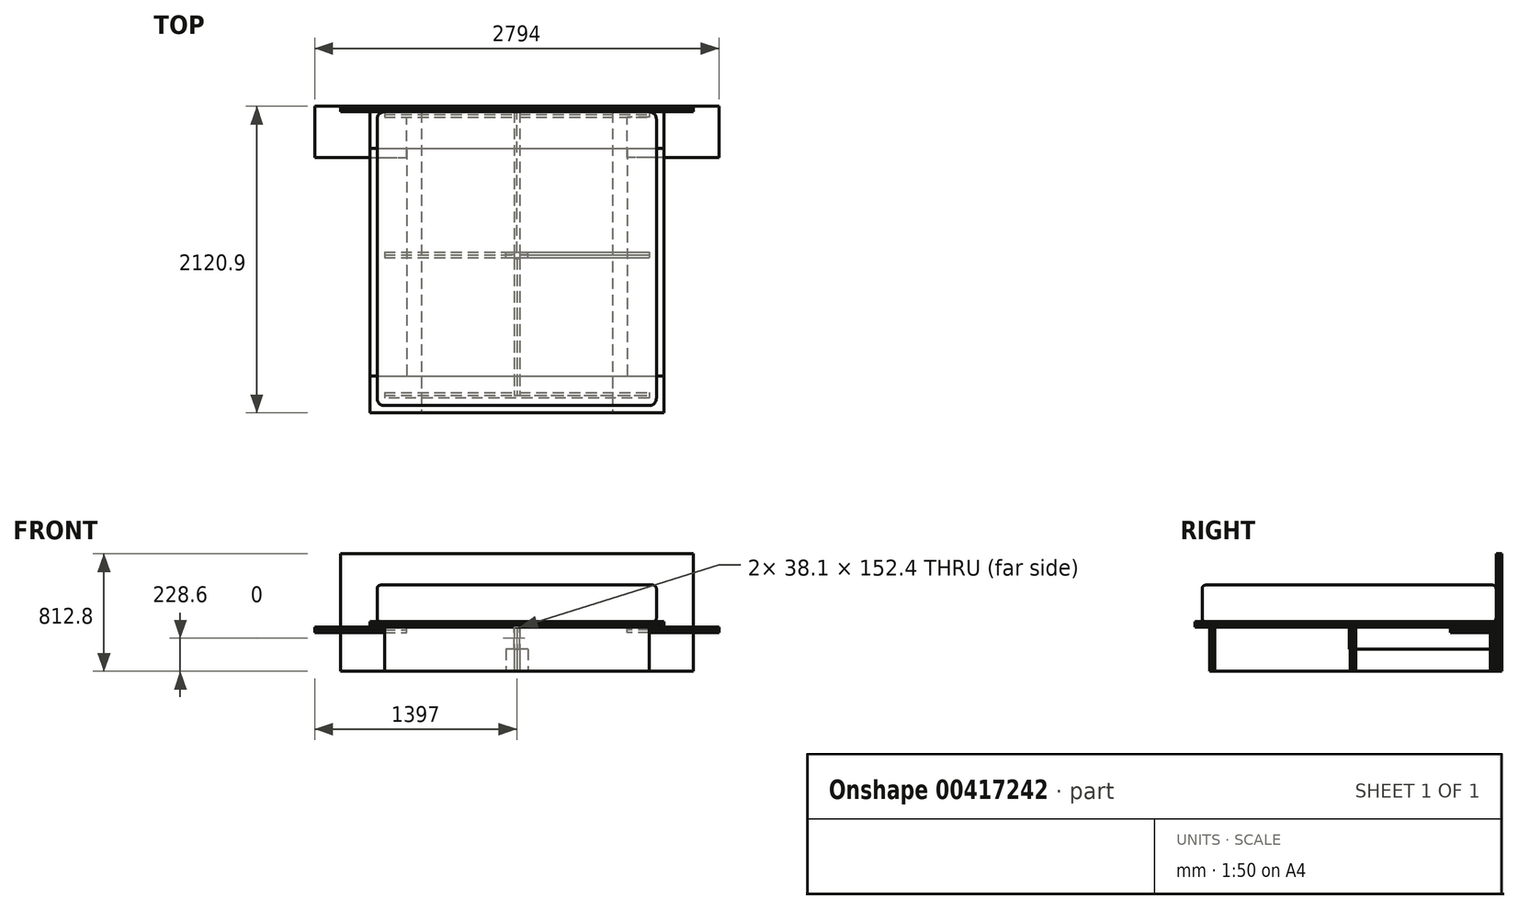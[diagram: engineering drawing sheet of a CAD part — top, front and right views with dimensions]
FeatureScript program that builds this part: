
annotation { "Feature Type Name" : "Feature", "Feature Type Description" : "" }
export const myFeature = defineFeature(function(context is Context, id is Id, definition is map)
    precondition{}
    {
        {
            var Q0;
            Q0=qCreatedBy(makeId("Top.planeOp"),FACE);
            var sketch = newSketch(context, id + "F0", { "sketchPlane" : qUnion([Q0])});
            skLineSegment(sketch, "E0.bottom", {"start": v(-965.2, 1016) * mm, "end": v(965.2, 1016) * mm});
            skLineSegment(sketch, "E0.top", {"start": v(-965.2, -1016) * mm, "end": v(965.2, -1016) * mm});
            skLineSegment(sketch, "E0.left", {"start": v(-965.2, 1016) * mm, "end": v(-965.2, -1016) * mm});
            skLineSegment(sketch, "E0.right", {"start": v(965.2, 1016) * mm, "end": v(965.2, -1016) * mm});
            skPoint(sketch, "E0.middle", {"position": v(0, 0) * mm});
            skLineSegment(sketch, "E1", {"start": v(0, 1016) * mm, "end": v(0, -1016) * mm, "construction": true});
            skSolve(sketch);
        }
        {
            var Q0;
            Q0=qCreatedBy(makeId("Top.planeOp"),FACE);
            var sketch = newSketch(context, id + "F1", { "sketchPlane" : qUnion([Q0])});
            skLineSegment(sketch, "E2.bottom", {"start": v(-1219.2, 1035.05) * mm, "end": v(1219.2, 1035.05) * mm});
            skLineSegment(sketch, "E2.top", {"start": v(-1219.2, 1016) * mm, "end": v(1219.2, 1016) * mm});
            skLineSegment(sketch, "E2.left", {"start": v(-1219.2, 1035.05) * mm, "end": v(-1219.2, 1016) * mm});
            skLineSegment(sketch, "E2.right", {"start": v(1219.2, 1035.05) * mm, "end": v(1219.2, 1016) * mm});
            skLineSegment(sketch, "E3", {"start": v(0, 1035.05) * mm, "end": v(0, 1016) * mm, "construction": true});
            skLineSegment(sketch, "E4.top", {"start": v(-1219.2, 1054.1) * mm, "end": v(1219.2, 1054.1) * mm});
            skLineSegment(sketch, "E4.left", {"start": v(-1219.2, 1035.05) * mm, "end": v(-1219.2, 1054.1) * mm});
            skLineSegment(sketch, "E4.right", {"start": v(1219.2, 1035.05) * mm, "end": v(1219.2, 1054.1) * mm});
            skSolve(sketch);
        }
        {
            var Q0;
            Q0=qCreatedBy(makeId("Top.planeOp"),FACE);
            var sketch = newSketch(context, id + "F2", { "sketchPlane" : qUnion([Q0])});
            skLineSegment(sketch, "E5.bottom", {"start": v(-1016, 1016) * mm, "end": v(1016, 1016) * mm});
            skLineSegment(sketch, "E5.top", {"start": v(-1016, -1066.8) * mm, "end": v(1016, -1066.8) * mm});
            skLineSegment(sketch, "E5.left", {"start": v(-1016, 1016) * mm, "end": v(-1016, -1066.8) * mm});
            skLineSegment(sketch, "E5.right", {"start": v(1016, 1016) * mm, "end": v(1016, -1066.8) * mm});
            skLineSegment(sketch, "E6", {"start": v(0, 1016) * mm, "end": v(0, -1066.8) * mm, "construction": true});
            skLineSegment(sketch, "E7", {"start": v(-1016, 762) * mm, "end": v(1016, 762) * mm, "construction": true});
            skLineSegment(sketch, "E8", {"start": v(-762, 1016) * mm, "end": v(-762, -1066.8) * mm, "construction": true});
            skLineSegment(sketch, "E9", {"start": v(-1016, -812.8) * mm, "end": v(1016, -812.8) * mm, "construction": true});
            skLineSegment(sketch, "E10", {"start": v(762, 1016) * mm, "end": v(762, -1066.8) * mm, "construction": true});
            skSolve(sketch);
        }
        {
            var Q0;
            Q0=qCreatedBy(makeId("Top.planeOp"),FACE);
            var sketch = newSketch(context, id + "F3", { "sketchPlane" : qUnion([Q0])});
            skLineSegment(sketch, "E11.bottom", {"start": v(-1397, 698.5) * mm, "end": v(-762, 698.5) * mm});
            skLineSegment(sketch, "E11.top", {"start": v(-1397, 1054.1) * mm, "end": v(-762, 1054.1) * mm});
            skLineSegment(sketch, "E11.left", {"start": v(-1397, 698.5) * mm, "end": v(-1397, 1054.1) * mm});
            skLineSegment(sketch, "E11.right", {"start": v(-762, 698.5) * mm, "end": v(-762, 1054.1) * mm});
            skLineSegment(sketch, "E12.MirrorCS", {"start": v(1397, 1054.1) * mm, "end": v(762, 1054.1) * mm});
            skLineSegment(sketch, "E13.MirrorCS", {"start": v(1397, 698.5) * mm, "end": v(1397, 1054.1) * mm});
            skLineSegment(sketch, "E14.MirrorCS", {"start": v(1397, 698.5) * mm, "end": v(762, 698.5) * mm});
            skLineSegment(sketch, "E15.MirrorCS", {"start": v(762, 698.5) * mm, "end": v(762, 1054.1) * mm});
            skSolve(sketch);
        }
        {
            var Q0;
            Q0=qCreatedBy(makeId("Top.planeOp"),FACE);
            var sketch = newSketch(context, id + "F4", { "sketchPlane" : qUnion([Q0])});
            skLineSegment(sketch, "E16.bottom", {"start": v(-914.4, 996.95) * mm, "end": v(914.4, 996.95) * mm});
            skLineSegment(sketch, "E16.top", {"start": v(-914.4, 1016) * mm, "end": v(914.4, 1016) * mm});
            skLineSegment(sketch, "E16.left", {"start": v(-914.4, 1016) * mm, "end": v(-914.4, 996.95) * mm});
            skLineSegment(sketch, "E16.right", {"start": v(914.4, 1016) * mm, "end": v(914.4, 996.95) * mm});
            skLineSegment(sketch, "E17", {"start": v(0, 1016) * mm, "end": v(0, 996.95) * mm, "construction": true});
            skLineSegment(sketch, "E18.top", {"start": v(-914.4, 977.9) * mm, "end": v(914.4, 977.9) * mm});
            skLineSegment(sketch, "E18.left", {"start": v(-914.4, 996.95) * mm, "end": v(-914.4, 977.9) * mm});
            skLineSegment(sketch, "E18.right", {"start": v(914.4, 996.95) * mm, "end": v(914.4, 977.9) * mm});
            skLineSegment(sketch, "E19.bottom", {"start": v(-914.4, 44.45) * mm, "end": v(914.4, 44.45) * mm});
            skLineSegment(sketch, "E19.top", {"start": v(-914.4, 25.4) * mm, "end": v(914.4, 25.4) * mm});
            skLineSegment(sketch, "E19.left", {"start": v(-914.4, 44.45) * mm, "end": v(-914.4, 25.4) * mm});
            skLineSegment(sketch, "E19.right", {"start": v(914.4, 44.45) * mm, "end": v(914.4, 25.4) * mm});
            skLineSegment(sketch, "E20.top", {"start": v(-914.4, 6.35) * mm, "end": v(914.4, 6.35) * mm});
            skLineSegment(sketch, "E20.left", {"start": v(-914.4, 25.4) * mm, "end": v(-914.4, 6.35) * mm});
            skLineSegment(sketch, "E20.right", {"start": v(914.4, 25.4) * mm, "end": v(914.4, 6.35) * mm});
            skLineSegment(sketch, "E21.bottom", {"start": v(-914.4, -927.1) * mm, "end": v(914.4, -927.1) * mm});
            skLineSegment(sketch, "E21.top", {"start": v(-914.4, -946.15) * mm, "end": v(914.4, -946.15) * mm});
            skLineSegment(sketch, "E21.left", {"start": v(-914.4, -927.1) * mm, "end": v(-914.4, -946.15) * mm});
            skLineSegment(sketch, "E21.right", {"start": v(914.4, -927.1) * mm, "end": v(914.4, -946.15) * mm});
            skLineSegment(sketch, "E22.bottom", {"start": v(914.4, -946.15) * mm, "end": v(-914.4, -946.15) * mm});
            skLineSegment(sketch, "E22.top", {"start": v(914.4, -965.2) * mm, "end": v(-914.4, -965.2) * mm});
            skLineSegment(sketch, "E22.left", {"start": v(914.4, -946.15) * mm, "end": v(914.4, -965.2) * mm});
            skLineSegment(sketch, "E22.right", {"start": v(-914.4, -946.15) * mm, "end": v(-914.4, -965.2) * mm});
            skSolve(sketch);
        }
        {
            var Q0;
            Q0=qCreatedBy(makeId("Top.planeOp"),FACE);
            var sketch = newSketch(context, id + "F5", { "sketchPlane" : qUnion([Q0])});
            skLineSegment(sketch, "E23.bottom", {"start": v(-19.05, 1016) * mm, "end": v(0, 1016) * mm});
            skLineSegment(sketch, "E23.top", {"start": v(-19.05, -946.15) * mm, "end": v(0, -946.15) * mm});
            skLineSegment(sketch, "E23.left", {"start": v(-19.05, 1016) * mm, "end": v(-19.05, -946.15) * mm});
            skLineSegment(sketch, "E23.right", {"start": v(0, 1016) * mm, "end": v(0, -946.15) * mm});
            skLineSegment(sketch, "E24.bottom", {"start": v(0, 1016) * mm, "end": v(19.05, 1016) * mm});
            skLineSegment(sketch, "E24.top", {"start": v(0, -946.15) * mm, "end": v(19.05, -946.15) * mm});
            skLineSegment(sketch, "E24.right", {"start": v(19.05, 1016) * mm, "end": v(19.05, -946.15) * mm});
            skSolve(sketch);
        }
        {
            var Q0;
            Q0=qCreatedBy(makeId("Top.planeOp"),FACE);
            cPlane(context, id + "F6", {"entities" : qUnion([Q0]), "cplaneType" : CPlaneType.OFFSET, "offset" : 304.8 * mm, "width" : 152.4 * mm, "height" : 152.4 * mm});
        }
        {
            var Q0;
            Q0=qCreatedBy(makeId("Top.planeOp"),FACE);
            var sketch = newSketch(context, id + "F7", { "sketchPlane" : qUnion([Q0])});
            skLineSegment(sketch, "E25.0", {"start": v(-1219.2, 1035.05) * mm, "end": v(1219.2, 1035.05) * mm});
            skLineSegment(sketch, "E25.1", {"start": v(-1219.2, 1016) * mm, "end": v(1219.2, 1016) * mm});
            skLineSegment(sketch, "E25.2", {"start": v(-1219.2, 1035.05) * mm, "end": v(-1219.2, 1016) * mm});
            skLineSegment(sketch, "E25.3", {"start": v(1219.2, 1035.05) * mm, "end": v(1219.2, 1016) * mm});
            skLineSegment(sketch, "E25.4", {"start": v(0, 1035.05) * mm, "end": v(0, 1016) * mm});
            skSolve(sketch);
        }
        {
            var Q0;
            Q0 = qSketchRegion(id + "F7", true);
            extrude(context, id + "F8", {"entities" : qUnion([Q0]), "depth" : 812.8 * mm});
        }
        {
            var Q0;
            Q0=qCreatedBy(makeId("Top.planeOp"),FACE);
            var sketch = newSketch(context, id + "F9", { "sketchPlane" : qUnion([Q0])});
            skLineSegment(sketch, "E26.0", {"start": v(-1219.2, 1035.05) * mm, "end": v(1219.2, 1035.05) * mm});
            skLineSegment(sketch, "E26.4", {"start": v(0, 1035.05) * mm, "end": v(0, 1016) * mm});
            skLineSegment(sketch, "E26.6", {"start": v(-1219.2, 1054.1) * mm, "end": v(1219.2, 1054.1) * mm});
            skLineSegment(sketch, "E26.7", {"start": v(-1219.2, 1035.05) * mm, "end": v(-1219.2, 1054.1) * mm});
            skLineSegment(sketch, "E26.8", {"start": v(1219.2, 1035.05) * mm, "end": v(1219.2, 1054.1) * mm});
            skSolve(sketch);
        }
        {
            var Q0;
            Q0 = qSketchRegion(id + "F9", true);
            var Q1;
            Q1=makeQuery(id+"F8.opExtrude","CAP_VERTEX",VERTEX,{"disambiguationData":[OSD([sQuery(id+"F7.wireOp",EDGE,"E25.0"),sQuery(id+"F7.wireOp",EDGE,"E25.3")])],"isStart":false});
            extrude(context, id + "F10", {"entities" : qUnion([Q0]), "endBound" : BoundingType.UP_TO_VERTEX, "endBoundEntityVertex" : qUnion([Q1]), "depth" : 25.4 * mm});
        }
        {
            var Q0;
            Q0=qCreatedBy(makeId("Top.planeOp"),FACE);
            var sketch = newSketch(context, id + "F11", { "sketchPlane" : qUnion([Q0])});
            skLineSegment(sketch, "E27.0", {"start": v(-914.4, 996.95) * mm, "end": v(-19.05, 996.95) * mm});
            skLineSegment(sketch, "E27.6", {"start": v(-914.4, 977.9) * mm, "end": v(-19.05, 977.9) * mm});
            skLineSegment(sketch, "E27.7", {"start": v(-914.4, 996.95) * mm, "end": v(-914.4, 977.9) * mm});
            skLineSegment(sketch, "E27.8", {"start": v(914.4, 996.95) * mm, "end": v(914.4, 977.9) * mm});
            skLineSegment(sketch, "E27.10", {"start": v(-914.4, 25.4) * mm, "end": v(914.4, 25.4) * mm});
            skLineSegment(sketch, "E27.14", {"start": v(-914.4, 6.35) * mm, "end": v(914.4, 6.35) * mm});
            skLineSegment(sketch, "E27.15", {"start": v(-914.4, 25.4) * mm, "end": v(-914.4, 6.35) * mm});
            skLineSegment(sketch, "E27.16", {"start": v(914.4, 25.4) * mm, "end": v(914.4, 6.35) * mm});
            skLineSegment(sketch, "E27.18", {"start": v(-914.4, -946.15) * mm, "end": v(914.4, -946.15) * mm});
            skLineSegment(sketch, "E27.22", {"start": v(914.4, -965.2) * mm, "end": v(-914.4, -965.2) * mm});
            skLineSegment(sketch, "E27.23", {"start": v(914.4, -946.15) * mm, "end": v(914.4, -965.2) * mm});
            skLineSegment(sketch, "E27.24", {"start": v(-914.4, -946.15) * mm, "end": v(-914.4, -965.2) * mm});
            skLineSegment(sketch, "E28.0", {"start": v(-19.05, 996.95) * mm, "end": v(-19.05, 977.9) * mm});
            skLineSegment(sketch, "E28.1", {"start": v(19.05, 996.95) * mm, "end": v(19.05, 977.9) * mm});
            skPoint(sketch, "E29.orphan", {"position": v(-19.05, 1016) * mm});
            skPoint(sketch, "E30.orphan", {"position": v(19.05, 1016) * mm});
            skLineSegment(sketch, "E31.trimOffspring", {"start": v(19.05, 996.95) * mm, "end": v(914.4, 996.95) * mm});
            skLineSegment(sketch, "E32.trimOffspring", {"start": v(19.05, 977.9) * mm, "end": v(914.4, 977.9) * mm});
            skSolve(sketch);
        }
        {
            var Q0;
            Q0 = qSketchRegion(id + "F11", true);
            var Q1;
            Q1=qCreatedBy(id+"F6.planeOp",FACE);
            extrude(context, id + "F12", {"entities" : qUnion([Q0]), "endBound" : BoundingType.UP_TO_SURFACE, "endBoundEntityFace" : qUnion([Q1]), "depth" : 25.4 * mm});
        }
        {
            var Q0;
            Q0=qCreatedBy(makeId("Top.planeOp"),FACE);
            var sketch = newSketch(context, id + "F13", { "sketchPlane" : qUnion([Q0])});
            skLineSegment(sketch, "E33.0", {"start": v(-914.4, 996.95) * mm, "end": v(-19.05, 996.95) * mm});
            skLineSegment(sketch, "E33.1", {"start": v(-914.4, 1016) * mm, "end": v(-19.05, 1016) * mm});
            skLineSegment(sketch, "E33.2", {"start": v(-914.4, 1016) * mm, "end": v(-914.4, 996.95) * mm});
            skLineSegment(sketch, "E33.3", {"start": v(914.4, 1016) * mm, "end": v(914.4, 996.95) * mm});
            skLineSegment(sketch, "E33.9", {"start": v(-914.4, 44.45) * mm, "end": v(914.4, 44.45) * mm});
            skLineSegment(sketch, "E33.10", {"start": v(-914.4, 25.4) * mm, "end": v(914.4, 25.4) * mm});
            skLineSegment(sketch, "E33.11", {"start": v(-914.4, 44.45) * mm, "end": v(-914.4, 25.4) * mm});
            skLineSegment(sketch, "E33.12", {"start": v(914.4, 44.45) * mm, "end": v(914.4, 25.4) * mm});
            skLineSegment(sketch, "E33.17", {"start": v(-914.4, -927.1) * mm, "end": v(-19.05, -927.1) * mm});
            skLineSegment(sketch, "E33.18", {"start": v(-914.4, -946.15) * mm, "end": v(-19.05, -946.15) * mm});
            skLineSegment(sketch, "E33.19", {"start": v(-914.4, -927.1) * mm, "end": v(-914.4, -946.15) * mm});
            skLineSegment(sketch, "E33.20", {"start": v(914.4, -927.1) * mm, "end": v(914.4, -946.15) * mm});
            skLineSegment(sketch, "E34.0", {"start": v(-19.05, 1016) * mm, "end": v(-19.05, 996.95) * mm});
            skLineSegment(sketch, "E34.1", {"start": v(19.05, 1016) * mm, "end": v(19.05, 996.95) * mm});
            skLineSegment(sketch, "E35.trimOffspring", {"start": v(19.05, -927.1) * mm, "end": v(914.4, -927.1) * mm});
            skLineSegment(sketch, "E36.trimOffspring", {"start": v(19.05, -946.15) * mm, "end": v(914.4, -946.15) * mm});
            skLineSegment(sketch, "E37.trimOffspring", {"start": v(19.05, -927.1) * mm, "end": v(19.05, -946.15) * mm});
            skLineSegment(sketch, "E38.trimOffspring", {"start": v(-19.05, -927.1) * mm, "end": v(-19.05, -946.15) * mm});
            skLineSegment(sketch, "E39.trimOffspring", {"start": v(19.05, 996.95) * mm, "end": v(914.4, 996.95) * mm});
            skLineSegment(sketch, "E40.trimOffspring", {"start": v(19.05, 1016) * mm, "end": v(914.4, 1016) * mm});
            skSolve(sketch);
        }
        {
            var Q0;
            Q0 = qSketchRegion(id + "F13", true);
            var Q1;
            Q1=qCreatedBy(id+"F6.planeOp",FACE);
            extrude(context, id + "F14", {"entities" : qUnion([Q0]), "endBound" : BoundingType.UP_TO_SURFACE, "endBoundEntityFace" : qUnion([Q1]), "depth" : 25.4 * mm});
        }
        {
            var Q0;
            Q0=qCreatedBy(makeId("Top.planeOp"),FACE);
            var sketch = newSketch(context, id + "F15", { "sketchPlane" : qUnion([Q0])});
            skLineSegment(sketch, "E41.0", {"start": v(-19.05, 1016) * mm, "end": v(0, 1016) * mm});
            skLineSegment(sketch, "E41.1", {"start": v(-19.05, -946.15) * mm, "end": v(0, -946.15) * mm});
            skLineSegment(sketch, "E41.2", {"start": v(-19.05, 1016) * mm, "end": v(-19.05, -946.15) * mm});
            skLineSegment(sketch, "E41.3", {"start": v(0, 1016) * mm, "end": v(0, -946.15) * mm});
            skSolve(sketch);
        }
        {
            var Q0;
            Q0 = qSketchRegion(id + "F15", true);
            var Q1;
            Q1=qCreatedBy(id+"F6.planeOp",FACE);
            extrude(context, id + "F16", {"entities" : qUnion([Q0]), "endBound" : BoundingType.UP_TO_SURFACE, "endBoundEntityFace" : qUnion([Q1]), "depth" : 25.4 * mm});
        }
        {
            var Q0;
            Q0=qCreatedBy(makeId("Top.planeOp"),FACE);
            var sketch = newSketch(context, id + "F17", { "sketchPlane" : qUnion([Q0])});
            skLineSegment(sketch, "E42.3", {"start": v(0, 1016) * mm, "end": v(0, -946.15) * mm});
            skLineSegment(sketch, "E42.4", {"start": v(0, 1016) * mm, "end": v(19.05, 1016) * mm});
            skLineSegment(sketch, "E42.5", {"start": v(0, -946.15) * mm, "end": v(19.05, -946.15) * mm});
            skLineSegment(sketch, "E42.7", {"start": v(19.05, 1016) * mm, "end": v(19.05, -946.15) * mm});
            skSolve(sketch);
        }
        {
            var Q0;
            Q0 = qSketchRegion(id + "F17", true);
            var Q1;
            Q1=qCreatedBy(id+"F6.planeOp",FACE);
            extrude(context, id + "F18", {"entities" : qUnion([Q0]), "endBound" : BoundingType.UP_TO_SURFACE, "endBoundEntityFace" : qUnion([Q1]), "depth" : 25.4 * mm});
        }
        {
            var Q0;
            Q0=qCreatedBy(makeId("Front.planeOp"),FACE);
            var sketch = newSketch(context, id + "F19", { "sketchPlane" : qUnion([Q0])});
            skLineSegment(sketch, "E43", {"start": v(0, 0) * mm, "end": v(0, 304.8) * mm, "construction": true});
            skLineSegment(sketch, "E44.bottom", {"start": v(-19.05, 304.8) * mm, "end": v(19.05, 304.8) * mm});
            skLineSegment(sketch, "E44.top", {"start": v(-19.05, 152.4) * mm, "end": v(19.05, 152.4) * mm});
            skLineSegment(sketch, "E44.left", {"start": v(-19.05, 304.8) * mm, "end": v(-19.05, 152.4) * mm});
            skLineSegment(sketch, "E44.right", {"start": v(19.05, 304.8) * mm, "end": v(19.05, 152.4) * mm});
            skLineSegment(sketch, "E45", {"start": v(0, 304.8) * mm, "end": v(0, 152.4) * mm, "construction": true});
            skSolve(sketch);
        }
        {
            var Q0;
            Q0 = qSketchRegion(id + "F19", true);
            extrude(context, id + "F20", {"entities" : qUnion([Q0]), "operationType" : NewBodyOperationType.REMOVE, "endBound" : BoundingType.THROUGH_ALL, "oppositeDirection" : true, "depth" : 25.4 * mm});
        }
        {
            var Q0;
            Q0=qCreatedBy(makeId("Right.planeOp"),FACE);
            var sketch = newSketch(context, id + "F21", { "sketchPlane" : qUnion([Q0])});
            skLineSegment(sketch, "E46.bottom", {"start": v(6.35, 152.4) * mm, "end": v(44.45, 152.4) * mm});
            skLineSegment(sketch, "E46.top", {"start": v(6.35, 0) * mm, "end": v(44.45, 0) * mm});
            skLineSegment(sketch, "E46.left", {"start": v(6.35, 152.4) * mm, "end": v(6.35, 0) * mm});
            skLineSegment(sketch, "E46.right", {"start": v(44.45, 152.4) * mm, "end": v(44.45, 0) * mm});
            skSolve(sketch);
        }
        {
            var Q0;
            Q0 = qSketchRegion(id + "F21", true);
            extrude(context, id + "F22", {"entities" : qUnion([Q0]), "operationType" : NewBodyOperationType.REMOVE, "endBound" : BoundingType.SYMMETRIC, "oppositeDirection" : true, "depth" : 152.4 * mm});
        }
        {
            var Q0;
            Q0=qCreatedBy(id+"F6.planeOp",FACE);
            var sketch = newSketch(context, id + "F23", { "sketchPlane" : qUnion([Q0])});
            skLineSegment(sketch, "E47.0", {"start": v(-660.4, 1016) * mm, "end": v(660.4, 1016) * mm});
            skLineSegment(sketch, "E47.1", {"start": v(-660.4, -1066.8) * mm, "end": v(660.4, -1066.8) * mm});
            skLineSegment(sketch, "E47.5", {"start": v(-660.4, 762) * mm, "end": v(660.4, 762) * mm});
            skLineSegment(sketch, "E47.7", {"start": v(-660.4, -812.8) * mm, "end": v(660.4, -812.8) * mm});
            skPoint(sketch, "E48.orphan", {"position": v(-1016, 762) * mm});
            skPoint(sketch, "E49.orphan", {"position": v(-1016, 1016) * mm});
            skPoint(sketch, "E50.orphan", {"position": v(1016, 1016) * mm});
            skPoint(sketch, "E51.orphan", {"position": v(1016, 762) * mm});
            skPoint(sketch, "E52.orphan", {"position": v(1016, -812.8) * mm});
            skPoint(sketch, "E53.orphan", {"position": v(1016, -1066.8) * mm});
            skPoint(sketch, "E54.orphan", {"position": v(-1016, -812.8) * mm});
            skPoint(sketch, "E55.orphan", {"position": v(-1016, -1066.8) * mm});
            skLineSegment(sketch, "E56", {"start": v(-660.4, 1016) * mm, "end": v(-660.4, 762) * mm});
            skPoint(sketch, "E47.6.start.orphan", {"position": v(-762, 1016) * mm});
            skPoint(sketch, "E57.orphan", {"position": v(-762, -1066.8) * mm});
            skLineSegment(sketch, "E58.trimOffspring", {"start": v(-660.4, -812.8) * mm, "end": v(-660.4, -1066.8) * mm});
            skLineSegment(sketch, "E59", {"start": v(660.4, 1016) * mm, "end": v(660.4, 762) * mm});
            skPoint(sketch, "E47.8.start.orphan", {"position": v(762, 1016) * mm});
            skPoint(sketch, "E60.orphan", {"position": v(762, -1066.8) * mm});
            skLineSegment(sketch, "E61.trimOffspring", {"start": v(660.4, -812.8) * mm, "end": v(660.4, -1066.8) * mm});
            skSolve(sketch);
        }
        {
            var Q0;
            Q0 = qSketchRegion(id + "F23", true);
            extrude(context, id + "F24", {"entities" : qUnion([Q0]), "depth" : 19.05 * mm});
        }
        {
            var Q0;
            Q0=qCreatedBy(id+"F6.planeOp",FACE);
            var sketch = newSketch(context, id + "F25", { "sketchPlane" : qUnion([Q0])});
            skLineSegment(sketch, "E62.bottom", {"start": v(-1016, 1016) * mm, "end": v(-660.4, 1016) * mm});
            skLineSegment(sketch, "E62.top", {"start": v(-1016, -1066.8) * mm, "end": v(-660.4, -1066.8) * mm});
            skLineSegment(sketch, "E62.left", {"start": v(-1016, 1016) * mm, "end": v(-1016, -1066.8) * mm});
            skLineSegment(sketch, "E62.right", {"start": v(-660.4, 1016) * mm, "end": v(-660.4, -1066.8) * mm});
            skLineSegment(sketch, "E63.bottom", {"start": v(660.4, 1016) * mm, "end": v(1016, 1016) * mm});
            skLineSegment(sketch, "E63.top", {"start": v(660.4, -1066.8) * mm, "end": v(1016, -1066.8) * mm});
            skLineSegment(sketch, "E63.left", {"start": v(660.4, 1016) * mm, "end": v(660.4, -1066.8) * mm});
            skLineSegment(sketch, "E63.right", {"start": v(1016, 1016) * mm, "end": v(1016, -1066.8) * mm});
            skSolve(sketch);
        }
        {
            var Q0;
            Q0 = qSketchRegion(id + "F25", true);
            extrude(context, id + "F26", {"entities" : qUnion([Q0]), "depth" : 19.05 * mm});
        }
        {
            var Q0;
            Q0=makeQuery(id+"F26.opExtrude","CAP_FACE",FACE,{"disambiguationData":[OSD([sQuery(id+"F25.wireOp",EDGE,"E62.bottom"),sQuery(id+"F25.wireOp",EDGE,"E62.top"),sQuery(id+"F25.wireOp",EDGE,"E62.left"),sQuery(id+"F25.wireOp",EDGE,"E62.right")])],"isStart":false});
            var sketch = newSketch(context, id + "F27", { "sketchPlane" : qUnion([Q0])});
            skLineSegment(sketch, "E64.bottom", {"start": v(-1016, 1016) * mm, "end": v(1016, 1016) * mm});
            skLineSegment(sketch, "E64.top", {"start": v(-1016, 762) * mm, "end": v(1016, 762) * mm});
            skLineSegment(sketch, "E64.left", {"start": v(-1016, 1016) * mm, "end": v(-1016, 762) * mm});
            skLineSegment(sketch, "E64.right", {"start": v(1016, 1016) * mm, "end": v(1016, 762) * mm});
            skLineSegment(sketch, "E65.bottom", {"start": v(-1016, -1066.8) * mm, "end": v(1016, -1066.8) * mm});
            skLineSegment(sketch, "E65.top", {"start": v(-1016, -812.8) * mm, "end": v(1016, -812.8) * mm});
            skLineSegment(sketch, "E65.left", {"start": v(-1016, -1066.8) * mm, "end": v(-1016, -812.8) * mm});
            skLineSegment(sketch, "E65.right", {"start": v(1016, -1066.8) * mm, "end": v(1016, -812.8) * mm});
            skSolve(sketch);
        }
        {
            var Q0;
            Q0 = qSketchRegion(id + "F27", true);
            extrude(context, id + "F28", {"entities" : qUnion([Q0]), "depth" : 19.05 * mm});
        }
        {
            var Q0;
            Q0=makeQuery(id+"F26.opExtrude","CAP_FACE",FACE,{"disambiguationData":[OSD([sQuery(id+"F25.wireOp",EDGE,"E62.bottom"),sQuery(id+"F25.wireOp",EDGE,"E62.top"),sQuery(id+"F25.wireOp",EDGE,"E62.left"),sQuery(id+"F25.wireOp",EDGE,"E62.right")])],"isStart":false});
            var sketch = newSketch(context, id + "F29", { "sketchPlane" : qUnion([Q0])});
            skLineSegment(sketch, "E66.bottom", {"start": v(-1016, 762) * mm, "end": v(-762, 762) * mm});
            skLineSegment(sketch, "E66.top", {"start": v(-1016, -812.8) * mm, "end": v(-762, -812.8) * mm});
            skLineSegment(sketch, "E66.left", {"start": v(-1016, 762) * mm, "end": v(-1016, -812.8) * mm});
            skLineSegment(sketch, "E66.right", {"start": v(-762, 762) * mm, "end": v(-762, -812.8) * mm});
            skLineSegment(sketch, "E67.bottom", {"start": v(762, 762) * mm, "end": v(1016, 762) * mm});
            skLineSegment(sketch, "E67.top", {"start": v(762, -812.8) * mm, "end": v(1016, -812.8) * mm});
            skLineSegment(sketch, "E67.left", {"start": v(762, 762) * mm, "end": v(762, -812.8) * mm});
            skLineSegment(sketch, "E67.right", {"start": v(1016, 762) * mm, "end": v(1016, -812.8) * mm});
            skSolve(sketch);
        }
        {
            var Q0;
            Q0 = qSketchRegion(id + "F29", true);
            extrude(context, id + "F30", {"entities" : qUnion([Q0]), "depth" : 19.05 * mm});
        }
        {
            var Q0;
            Q0=qCreatedBy(id+"F6.planeOp",FACE);
            var sketch = newSketch(context, id + "F31", { "sketchPlane" : qUnion([Q0])});
            skLineSegment(sketch, "E68.0", {"start": v(-1397, 698.5) * mm, "end": v(-762, 698.5) * mm});
            skLineSegment(sketch, "E68.1", {"start": v(-1397, 1054.1) * mm, "end": v(-1219.2, 1054.1) * mm});
            skLineSegment(sketch, "E68.2", {"start": v(-1397, 698.5) * mm, "end": v(-1397, 1054.1) * mm});
            skLineSegment(sketch, "E68.3", {"start": v(-762, 698.5) * mm, "end": v(-762, 977.9) * mm});
            skLineSegment(sketch, "E69", {"start": v(-1219.2, 1054.1) * mm, "end": v(-1219.2, 1016) * mm});
            skLineSegment(sketch, "E70", {"start": v(-1219.2, 1016) * mm, "end": v(-914.4, 1016) * mm});
            skLineSegment(sketch, "E71", {"start": v(-914.4, 1016) * mm, "end": v(-914.4, 977.9) * mm});
            skLineSegment(sketch, "E72", {"start": v(-914.4, 977.9) * mm, "end": v(-762, 977.9) * mm});
            skPoint(sketch, "E73.orphan", {"position": v(-762, 1054.1) * mm});
            skLineSegment(sketch, "E74.MirrorCS", {"start": v(1397, 1054.1) * mm, "end": v(1219.2, 1054.1) * mm});
            skLineSegment(sketch, "E75.MirrorCS", {"start": v(1219.2, 1054.1) * mm, "end": v(1219.2, 1016) * mm});
            skLineSegment(sketch, "E76.MirrorCS", {"start": v(1219.2, 1016) * mm, "end": v(914.4, 1016) * mm});
            skLineSegment(sketch, "E77.MirrorCS", {"start": v(914.4, 1016) * mm, "end": v(914.4, 977.9) * mm});
            skLineSegment(sketch, "E78.MirrorCS", {"start": v(914.4, 977.9) * mm, "end": v(762, 977.9) * mm});
            skLineSegment(sketch, "E79.MirrorCS", {"start": v(762, 698.5) * mm, "end": v(762, 977.9) * mm});
            skLineSegment(sketch, "E80.MirrorCS", {"start": v(1397, 698.5) * mm, "end": v(762, 698.5) * mm});
            skLineSegment(sketch, "E81.MirrorCS", {"start": v(1397, 698.5) * mm, "end": v(1397, 1054.1) * mm});
            skSolve(sketch);
        }
        {
            var Q0;
            Q0 = qSketchRegion(id + "F31", true);
            extrude(context, id + "F32", {"entities" : qUnion([Q0]), "oppositeDirection" : true, "depth" : 19.05 * mm});
        }
        {
            var Q0;
            Q0=makeQuery(id+"F32.opExtrude","CAP_FACE",FACE,{"disambiguationData":[OSD([sQuery(id+"F31.wireOp",EDGE,"E74.MirrorCS"),sQuery(id+"F31.wireOp",EDGE,"E75.MirrorCS"),sQuery(id+"F31.wireOp",EDGE,"E76.MirrorCS"),sQuery(id+"F31.wireOp",EDGE,"E77.MirrorCS"),sQuery(id+"F31.wireOp",EDGE,"E78.MirrorCS"),sQuery(id+"F31.wireOp",EDGE,"E79.MirrorCS"),sQuery(id+"F31.wireOp",EDGE,"E80.MirrorCS"),sQuery(id+"F31.wireOp",EDGE,"E81.MirrorCS")])],"isStart":false});
            var sketch = newSketch(context, id + "F33", { "sketchPlane" : qUnion([Q0])});
            skLineSegment(sketch, "E82.0", {"start": v(-1397, -698.5) * mm, "end": v(-762, -698.5) * mm});
            skLineSegment(sketch, "E82.1", {"start": v(-1397, -1054.1) * mm, "end": v(-1219.2, -1054.1) * mm});
            skLineSegment(sketch, "E82.2", {"start": v(-1397, -698.5) * mm, "end": v(-1397, -1054.1) * mm});
            skLineSegment(sketch, "E82.3", {"start": v(-762, -698.5) * mm, "end": v(-762, -977.9) * mm});
            skLineSegment(sketch, "E82.4", {"start": v(-1219.2, -1054.1) * mm, "end": v(-1219.2, -1016) * mm});
            skLineSegment(sketch, "E82.5", {"start": v(-1219.2, -1016) * mm, "end": v(-914.4, -1016) * mm});
            skLineSegment(sketch, "E82.6", {"start": v(-914.4, -1016) * mm, "end": v(-914.4, -977.9) * mm});
            skLineSegment(sketch, "E82.7", {"start": v(-914.4, -977.9) * mm, "end": v(-762, -977.9) * mm});
            skPoint(sketch, "E82.8", {"position": v(-762, -1054.1) * mm});
            skPoint(sketch, "E82.9", {"position": v(-762, -1054.1) * mm});
            skLineSegment(sketch, "E82.10", {"start": v(1397, -1054.1) * mm, "end": v(1219.2, -1054.1) * mm});
            skLineSegment(sketch, "E82.11", {"start": v(1219.2, -1054.1) * mm, "end": v(1219.2, -1016) * mm});
            skLineSegment(sketch, "E82.12", {"start": v(1219.2, -1016) * mm, "end": v(914.4, -1016) * mm});
            skLineSegment(sketch, "E82.13", {"start": v(914.4, -1016) * mm, "end": v(914.4, -977.9) * mm});
            skLineSegment(sketch, "E82.14", {"start": v(914.4, -977.9) * mm, "end": v(762, -977.9) * mm});
            skLineSegment(sketch, "E82.15", {"start": v(762, -698.5) * mm, "end": v(762, -977.9) * mm});
            skLineSegment(sketch, "E82.16", {"start": v(1397, -698.5) * mm, "end": v(762, -698.5) * mm});
            skLineSegment(sketch, "E82.17", {"start": v(1397, -698.5) * mm, "end": v(1397, -1054.1) * mm});
            skSolve(sketch);
        }
        {
            var Q0;
            Q0 = qSketchRegion(id + "F33", true);
            extrude(context, id + "F34", {"entities" : qUnion([Q0]), "depth" : 19.05 * mm});
        }
        {
            var Q0;
            Q0=makeQuery(id+"F30.opExtrude","CAP_FACE",FACE,{"disambiguationData":[OSD([sQuery(id+"F29.wireOp",EDGE,"E66.bottom"),sQuery(id+"F29.wireOp",EDGE,"E66.top"),sQuery(id+"F29.wireOp",EDGE,"E66.left"),sQuery(id+"F29.wireOp",EDGE,"E66.right")])],"isStart":false});
            var sketch = newSketch(context, id + "F35", { "sketchPlane" : qUnion([Q0])});
            skLineSegment(sketch, "E83.0", {"start": v(-914.4, 1016) * mm, "end": v(914.4, 1016) * mm});
            skLineSegment(sketch, "E83.1", {"start": v(-914.4, -1016) * mm, "end": v(914.4, -1016) * mm});
            skLineSegment(sketch, "E83.2", {"start": v(-965.2, 965.2) * mm, "end": v(-965.2, -965.2) * mm});
            skLineSegment(sketch, "E83.3", {"start": v(965.2, 965.2) * mm, "end": v(965.2, -965.2) * mm});
            skPoint(sketch, "E83.4", {"position": v(0, 0) * mm});
            skLineSegment(sketch, "E83.5", {"start": v(0, 1016) * mm, "end": v(0, -1016) * mm});
            skPoint(sketch, "E84.visualSharp", {"position": v(-965.2, 1016) * mm});
            skArc(sketch, "E84.filletArc", {"start": v(-914.4, 1016) * mm, "mid": v(-950.32, 1001.12) * mm, "end": v(-965.2, 965.2) * mm});
            skPoint(sketch, "E85.visualSharp", {"position": v(965.2, 1016) * mm});
            skArc(sketch, "E85.filletArc", {"start": v(965.2, 965.2) * mm, "mid": v(950.32, 1001.12) * mm, "end": v(914.4, 1016) * mm});
            skPoint(sketch, "E86.visualSharp", {"position": v(965.2, -1016) * mm});
            skArc(sketch, "E86.filletArc", {"start": v(914.4, -1016) * mm, "mid": v(950.32, -1001.12) * mm, "end": v(965.2, -965.2) * mm});
            skPoint(sketch, "E87.visualSharp", {"position": v(-965.2, -1016) * mm});
            skArc(sketch, "E87.filletArc", {"start": v(-965.2, -965.2) * mm, "mid": v(-950.32, -1001.12) * mm, "end": v(-914.4, -1016) * mm});
            skSolve(sketch);
        }
        {
            var Q0;
            Q0 = qSketchRegion(id + "F35", true);
            extrude(context, id + "F36", {"entities" : qUnion([Q0]), "depth" : 254 * mm});
        }
        {
            var Q0;
            Q0=makeQuery(id+"F36.opExtrude","CAP_EDGE",EDGE,{"disambiguationData":[OSD([sQuery(id+"F35.wireOp",EDGE,"E83.1")])],"isStart":false});
            var Q1;
            Q1=makeQuery(id+"F36.opExtrude","CAP_EDGE",EDGE,{"disambiguationData":[OSD([sQuery(id+"F35.wireOp",EDGE,"E83.1")])],"isStart":true});
            fillet(context, id + "F37", {"entities" : qUnion([Q0, Q1]), "radius" : 25.4 * mm, "tangentPropagation" : true, "allowEdgeOverflow" : false});
        }
    });
